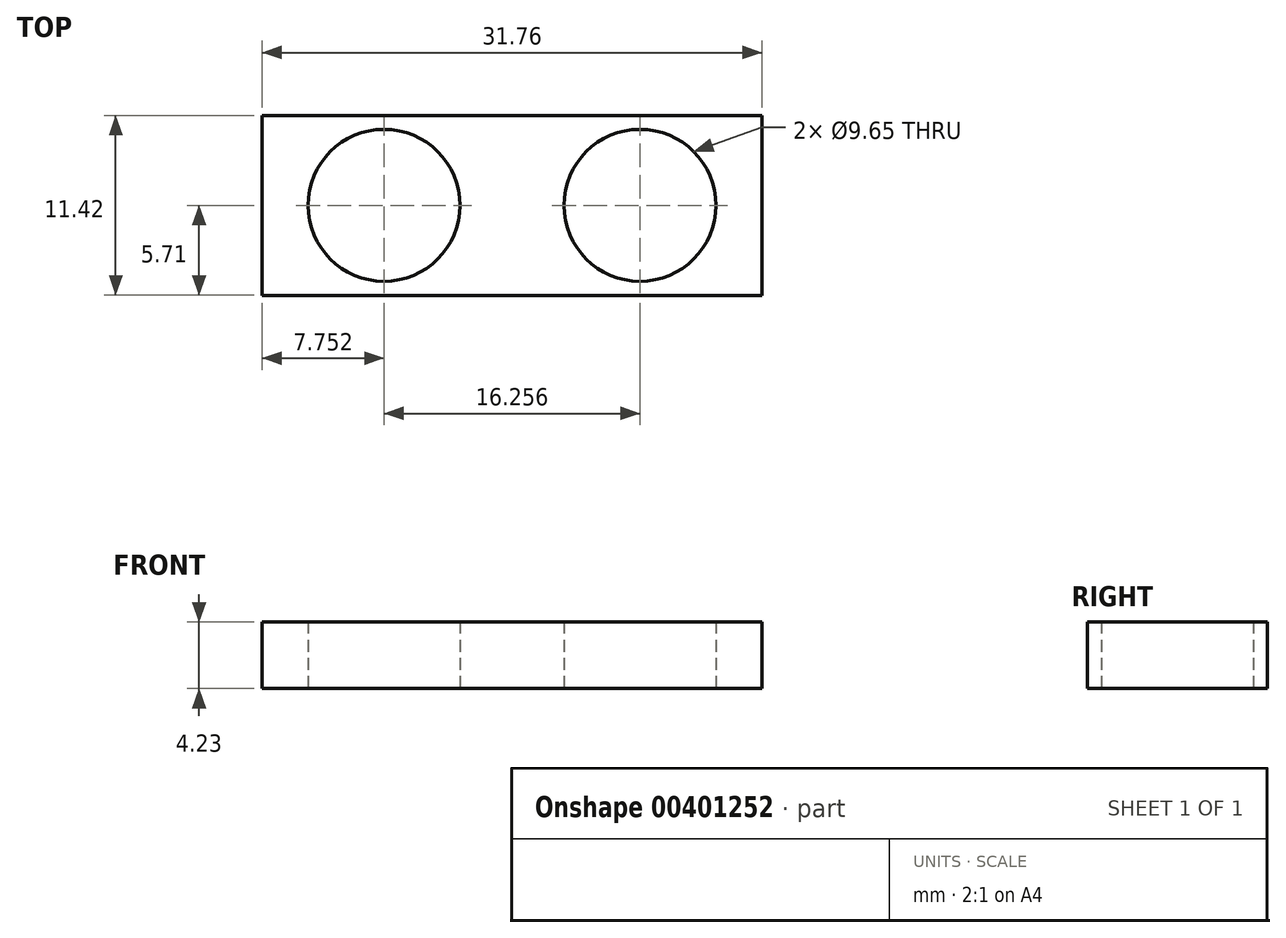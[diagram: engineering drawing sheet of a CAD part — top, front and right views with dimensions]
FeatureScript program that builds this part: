
annotation { "Feature Type Name" : "Feature", "Feature Type Description" : "" }
export const myFeature = defineFeature(function(context is Context, id is Id, definition is map)
    precondition{}
    {
        {
            var Q0;
            Q0=qCreatedBy(makeId("Top.planeOp"),FACE);
            var sketch = newSketch(context, id + "F0", { "sketchPlane" : qUnion([Q0])});
            skLineSegment(sketch, "E0.bottom", {"start": v(-15.87, 5.71) * mm, "end": v(15.88, 5.71) * mm});
            skLineSegment(sketch, "E0.top", {"start": v(-15.88, -5.72) * mm, "end": v(15.87, -5.72) * mm});
            skLineSegment(sketch, "E0.left", {"start": v(-15.88, 5.72) * mm, "end": v(-15.88, -5.71) * mm});
            skLineSegment(sketch, "E0.right", {"start": v(15.88, 5.71) * mm, "end": v(15.88, -5.72) * mm});
            skPoint(sketch, "E0.middle", {"position": v(0, 0) * mm});
            skCircle(sketch, "E1", {"center": v(-8.13, 0) * mm, "radius": 4.83 * mm});
            skCircle(sketch, "E2", {"center": v(8.13, 0) * mm, "radius": 4.83 * mm});
            skSolve(sketch);
        }
        {
            var Q0;
            Q0 = qSketchRegion(id + "F0", true);
            extrude(context, id + "F1", {"entities" : qUnion([Q0]), "depth" : 4.23 * mm});
        }
    });
